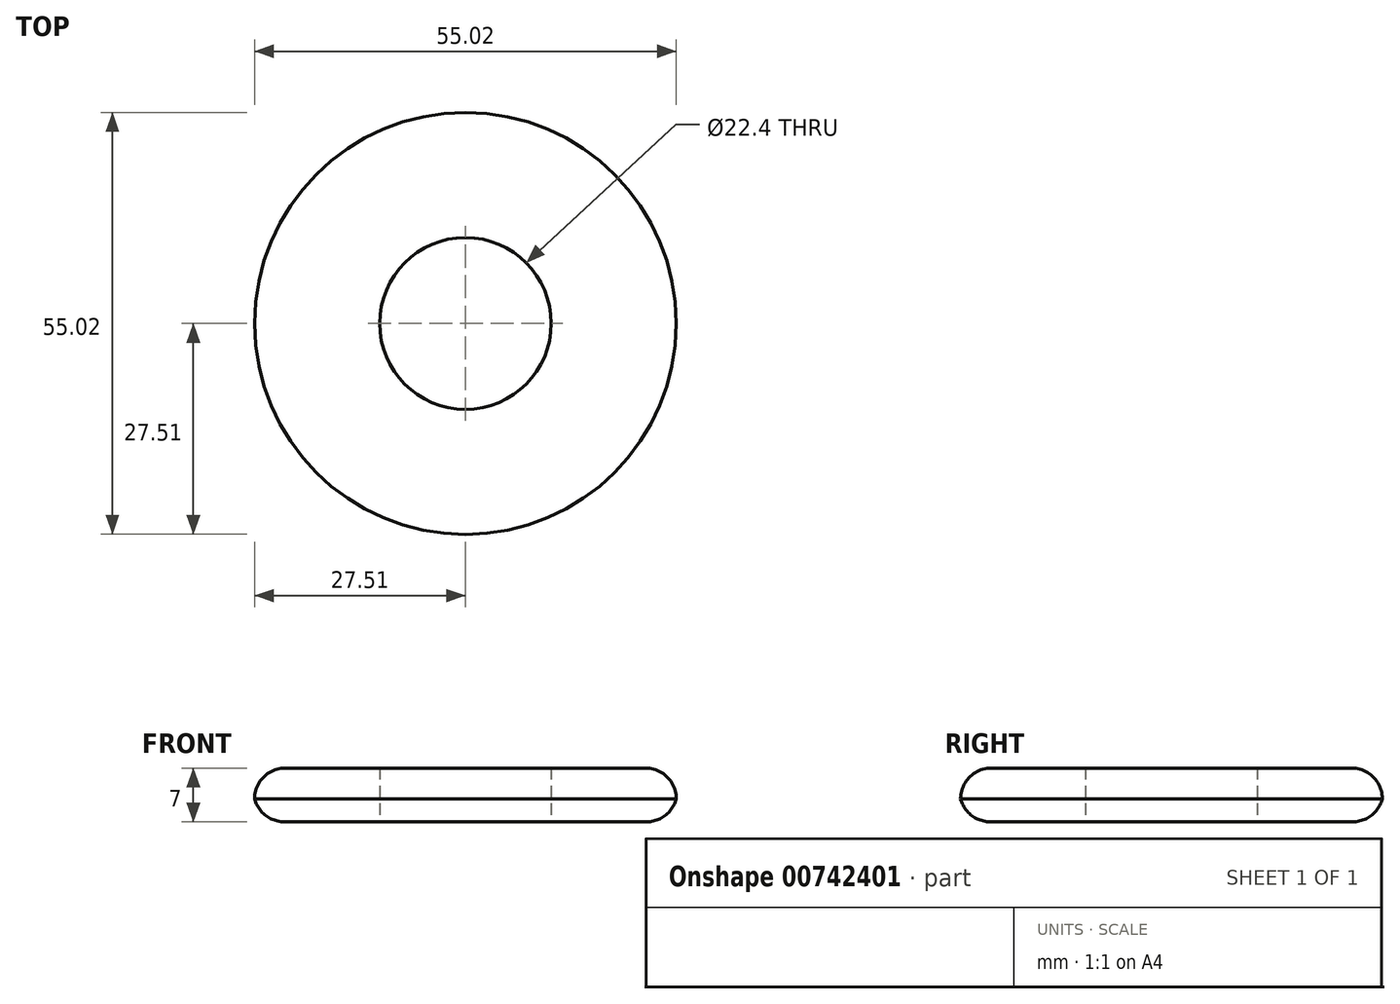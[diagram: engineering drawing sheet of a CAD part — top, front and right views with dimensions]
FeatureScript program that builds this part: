
annotation { "Feature Type Name" : "Feature", "Feature Type Description" : "" }
export const myFeature = defineFeature(function(context is Context, id is Id, definition is map)
    precondition{}
    {
        {
            var Q0;
            Q0=qCreatedBy(makeId("Top.planeOp"),FACE);
            var sketch = newSketch(context, id + "F0", { "sketchPlane" : qUnion([Q0])});
            skCircle(sketch, "E0", {"center": v(0, 0) * mm, "radius": 11.2 * mm});
            skCircle(sketch, "E1", {"center": v(0, 0) * mm, "radius": 27.51 * mm});
            skPoint(sketch, "E2.start.orphan", {"position": v(-23.9, 0) * mm});
            skPoint(sketch, "E3.end.orphan", {"position": v(0, -22.48) * mm});
            skPoint(sketch, "E4.end.orphan", {"position": v(24.02, 0) * mm});
            skPoint(sketch, "E4.start.orphan", {"position": v(0, 25.4) * mm});
            skSolve(sketch);
        }
        {
            var Q0;
            Q0 = qSketchRegion(id + "F0", true);
            extrude(context, id + "F1", {"entities" : qUnion([Q0]), "depth" : 7 * mm, "offsetDistance" : 25 * mm});
        }
        {
            var Q0;
            Q0=makeQuery(id+"F1.opExtrude","CAP_EDGE",EDGE,{"disambiguationData":[OSD([sQuery(id+"F0.wireOp",EDGE,"E1")])],"isStart":false});
            fillet(context, id + "F2", {"entities" : qUnion([Q0]), "radius" : 4 * mm, "tangentPropagation" : true, "allowEdgeOverflow" : false});
        }
        {
            var Q0;
            Q0=makeQuery(id+"F1.opExtrude","CAP_EDGE",EDGE,{"disambiguationData":[OSD([sQuery(id+"F0.wireOp",EDGE,"E1")])],"isStart":true});
            fillet(context, id + "F3", {"entities" : qUnion([Q0]), "radius" : 4 * mm, "tangentPropagation" : true, "allowEdgeOverflow" : false});
        }
    });
